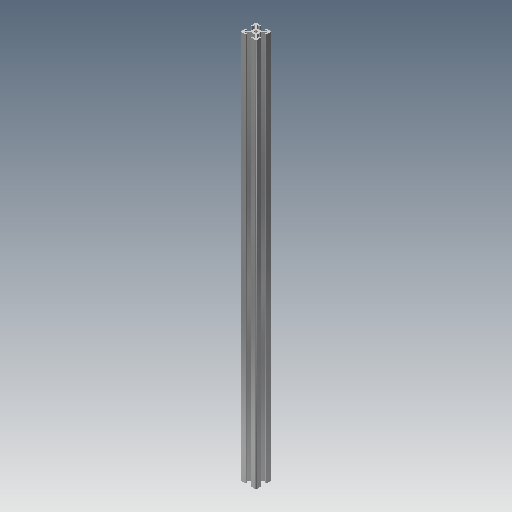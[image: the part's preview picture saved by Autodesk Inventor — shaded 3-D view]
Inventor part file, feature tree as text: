
AUTODESK INVENTOR PART (.ipt)
format: ipt  version: 2018.2 (Build 222227000, 227)  size: 161,280 bytes
history: native  units: mm
features: extrude x1, sketch x1
ambient origin geometry x8: Origin, YZ Plane, XZ Plane, XY Plane, X Axis, Y Axis, Z Axis, Center Point
bodies: Solid1 (feature_tree)
feature tree (2):
  extrude  "Extrusion1"  [1 undecoded]
  sketch  "Sketch1"  dims[d0=500.0mm d1=0.0mm]
note: 1 required parameter value undecoded (feature->parameter linkage not recoverable at this tier; creation-order binding heuristic only, values carry confidence <= 0.55)
